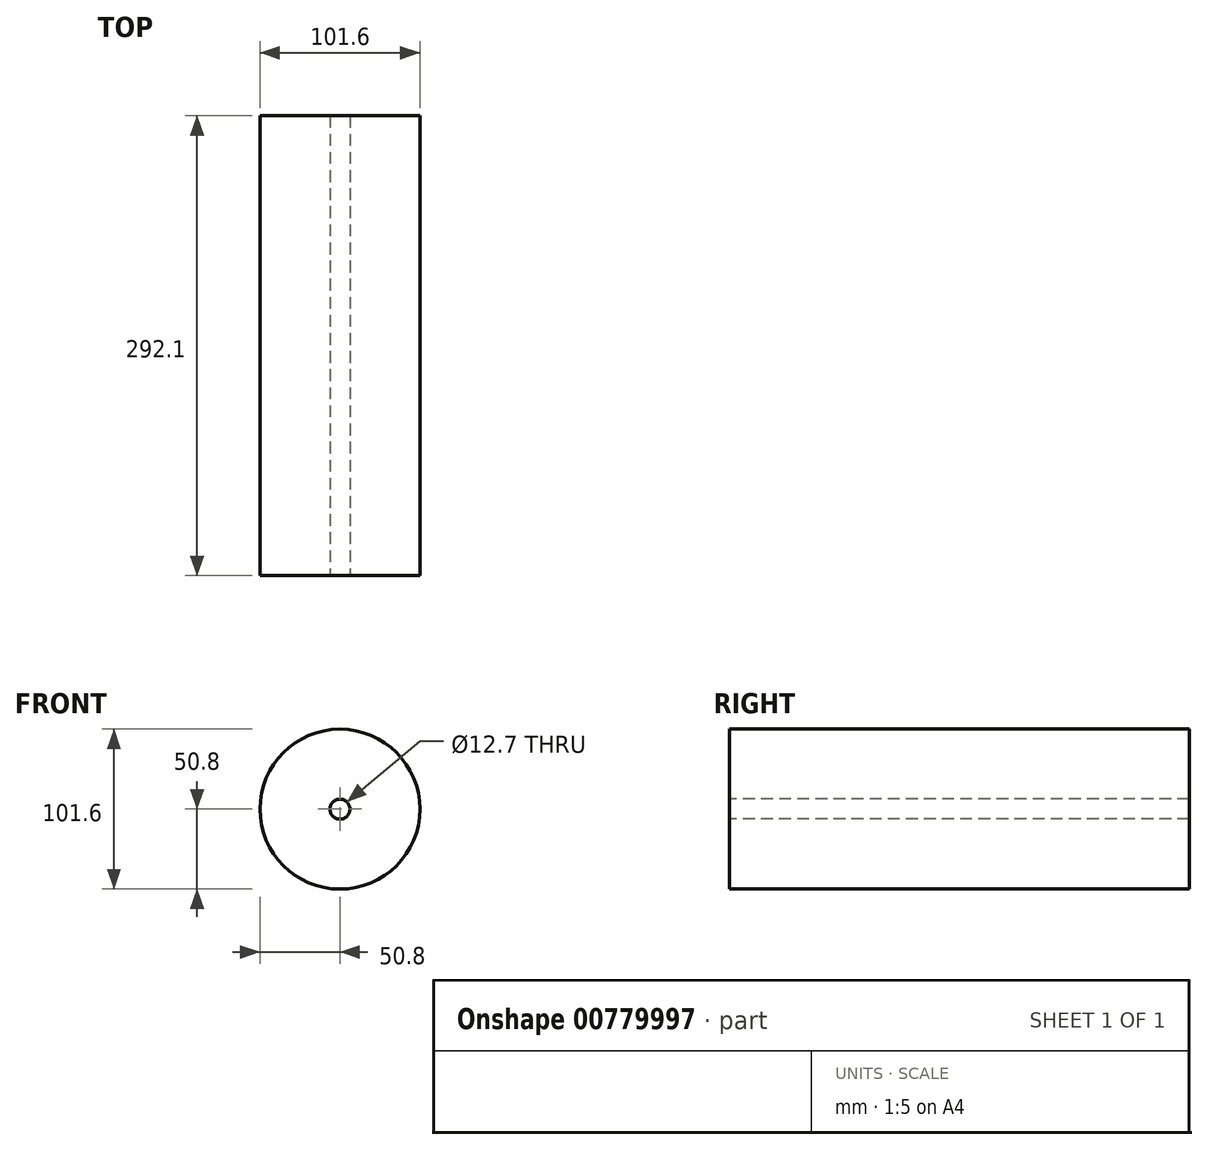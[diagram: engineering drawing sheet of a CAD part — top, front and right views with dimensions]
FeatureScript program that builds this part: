
annotation { "Feature Type Name" : "Feature", "Feature Type Description" : "" }
export const myFeature = defineFeature(function(context is Context, id is Id, definition is map)
    precondition{}
    {
        {
            var Q0;
            Q0=qCreatedBy(makeId("Front.planeOp"),FACE);
            var sketch = newSketch(context, id + "F0", { "sketchPlane" : qUnion([Q0])});
            skCircle(sketch, "E0", {"center": v(0, 0) * mm, "radius": 50.8 * mm});
            skSolve(sketch);
        }
        {
            var Q0;
            Q0 = qSketchRegion(id + "F0", true);
            var Q1;
            Q1=makeQuery(id+"F0.imprint","IMPRINT",FACE,{"disambiguationData":[TD([[makeQuery(id+"F0.imprint","IMPRINT",EDGE,{"derivedFrom":sQuery(id+"F0.wireOp",EDGE,"E0")}),1.0]])]});
            extrude(context, id + "F1", {"entities" : qUnion([Q0, Q1]), "depth" : 292.1 * mm, "offsetDistance" : 25.4 * mm});
        }
        {
            var Q0;
            Q0=makeQuery(id+"F1.opExtrude","CAP_FACE",FACE,{"disambiguationData":[OSD([sQuery(id+"F0.wireOp",EDGE,"E0")])],"isStart":false});
            var sketch = newSketch(context, id + "F2", { "sketchPlane" : qUnion([Q0])});
            skCircle(sketch, "E1", {"center": v(0, 0) * mm, "radius": 6.35 * mm});
            skSolve(sketch);
        }
        {
            var Q0;
            Q0 = qSketchRegion(id + "F2", true);
            extrude(context, id + "F3", {"entities" : qUnion([Q0]), "operationType" : NewBodyOperationType.REMOVE, "oppositeDirection" : true, "depth" : 292.1 * mm, "offsetDistance" : 25.4 * mm});
        }
    });
